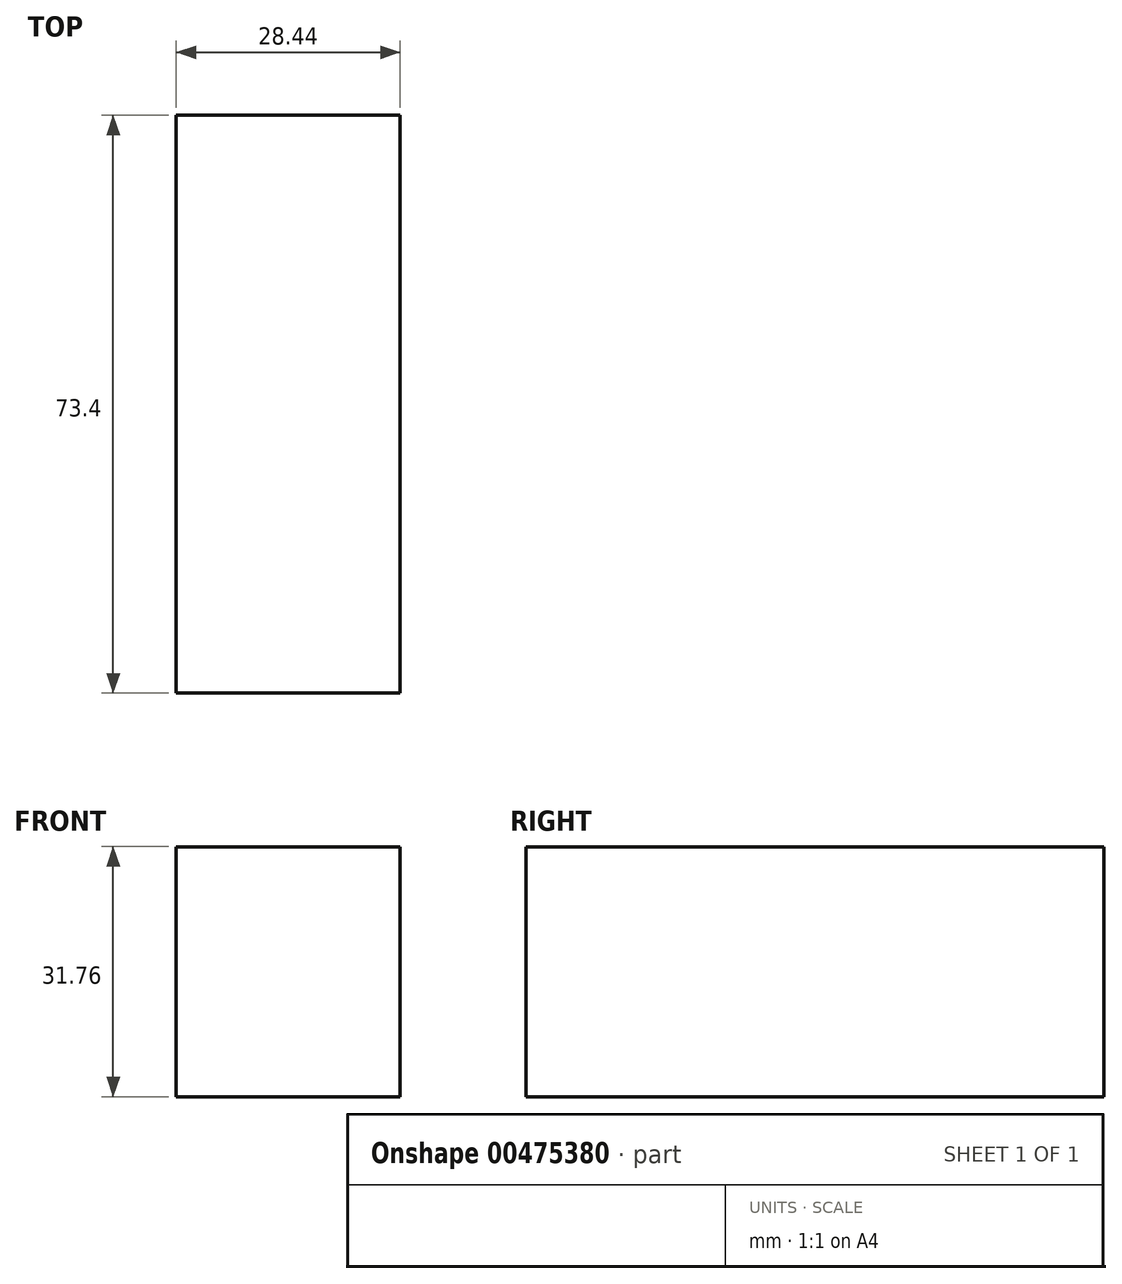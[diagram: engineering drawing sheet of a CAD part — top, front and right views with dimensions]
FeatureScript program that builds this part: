
annotation { "Feature Type Name" : "Feature", "Feature Type Description" : "" }
export const myFeature = defineFeature(function(context is Context, id is Id, definition is map)
    precondition{}
    {
        {
            var Q0;
            Q0=qCreatedBy(makeId("Right.planeOp"),FACE);
            var sketch = newSketch(context, id + "F0", { "sketchPlane" : qUnion([Q0])});
            skLineSegment(sketch, "E0.bottom", {"start": v(52.32, -44.45) * mm, "end": v(-52.32, -44.45) * mm});
            skLineSegment(sketch, "E0.top", {"start": v(52.32, 44.45) * mm, "end": v(-52.32, 44.45) * mm});
            skLineSegment(sketch, "E0.left", {"start": v(52.32, -44.45) * mm, "end": v(52.32, 44.45) * mm, "construction": true});
            skLineSegment(sketch, "E0.right", {"start": v(-52.32, -44.45) * mm, "end": v(-52.32, 44.45) * mm});
            skPoint(sketch, "E0.middle", {"position": v(0, 0) * mm});
            skCircle(sketch, "E1", {"center": v(-22.1, -30.23) * mm, "radius": 5.59 * mm});
            skCircle(sketch, "E2", {"center": v(1.78, -30.23) * mm, "radius": 5.59 * mm});
            skLineSegment(sketch, "E3", {"start": v(-22.1, -24.64) * mm, "end": v(1.78, -24.64) * mm});
            skLineSegment(sketch, "E4", {"start": v(1.78, -35.81) * mm, "end": v(-22.1, -35.81) * mm});
            skLineSegment(sketch, "E5", {"start": v(-22.1, -24.64) * mm, "end": v(-22.1, -35.81) * mm});
            skLineSegment(sketch, "E6", {"start": v(1.78, -24.64) * mm, "end": v(1.78, -35.81) * mm});
            skCircle(sketch, "E7", {"center": v(-22.1, 30.23) * mm, "radius": 5.59 * mm});
            skCircle(sketch, "E8", {"center": v(1.78, 30.23) * mm, "radius": 5.59 * mm});
            skLineSegment(sketch, "E9", {"start": v(-22.1, 35.81) * mm, "end": v(1.78, 35.81) * mm});
            skLineSegment(sketch, "E10", {"start": v(1.78, 24.64) * mm, "end": v(-22.1, 24.64) * mm});
            skLineSegment(sketch, "E11", {"start": v(-22.1, 35.81) * mm, "end": v(-22.1, 24.64) * mm});
            skLineSegment(sketch, "E12", {"start": v(1.78, 35.81) * mm, "end": v(1.78, 24.64) * mm});
            skLineSegment(sketch, "E13.bottom", {"start": v(-52.32, -15.88) * mm, "end": v(21.08, -15.88) * mm});
            skLineSegment(sketch, "E13.top", {"start": v(-52.32, 15.88) * mm, "end": v(21.08, 15.88) * mm});
            skLineSegment(sketch, "E13.left", {"start": v(-52.32, -15.88) * mm, "end": v(-52.32, 15.88) * mm});
            skLineSegment(sketch, "E13.right", {"start": v(21.08, -15.88) * mm, "end": v(21.08, 15.88) * mm});
            skLineSegment(sketch, "E14", {"start": v(52.32, -44.45) * mm, "end": v(23.75, -15.87) * mm});
            skLineSegment(sketch, "E15", {"start": v(52.32, 44.45) * mm, "end": v(23.75, 15.87) * mm});
            skLineSegment(sketch, "E16", {"start": v(21.08, 15.88) * mm, "end": v(23.75, 15.88) * mm});
            skLineSegment(sketch, "E17", {"start": v(21.08, -15.88) * mm, "end": v(23.75, -15.88) * mm});
            skLineSegment(sketch, "E18", {"start": v(17.27, 44.45) * mm, "end": v(17.27, 26.92) * mm});
            skLineSegment(sketch, "E19", {"start": v(17.27, -44.45) * mm, "end": v(17.27, -26.92) * mm});
            skLineSegment(sketch, "E20", {"start": v(34.8, 26.92) * mm, "end": v(17.27, 26.92) * mm});
            skLineSegment(sketch, "E21", {"start": v(34.8, -26.92) * mm, "end": v(17.27, -26.92) * mm});
            skSolve(sketch);
        }
        {
            var Q0;
            Q0=makeQuery(id+"F0.imprint","IMPRINT",FACE,{"disambiguationData":[TD([[makeQuery(id+"F0.imprint","IMPRINT",EDGE,{"derivedFrom":sQuery(id+"F0.wireOp",EDGE,"E13.bottom")}),1.0]])]});
            extrude(context, id + "F1", {"entities" : qUnion([Q0]), "endBound" : BoundingType.SYMMETRIC, "depth" : 28.45 * mm});
        }
    });
